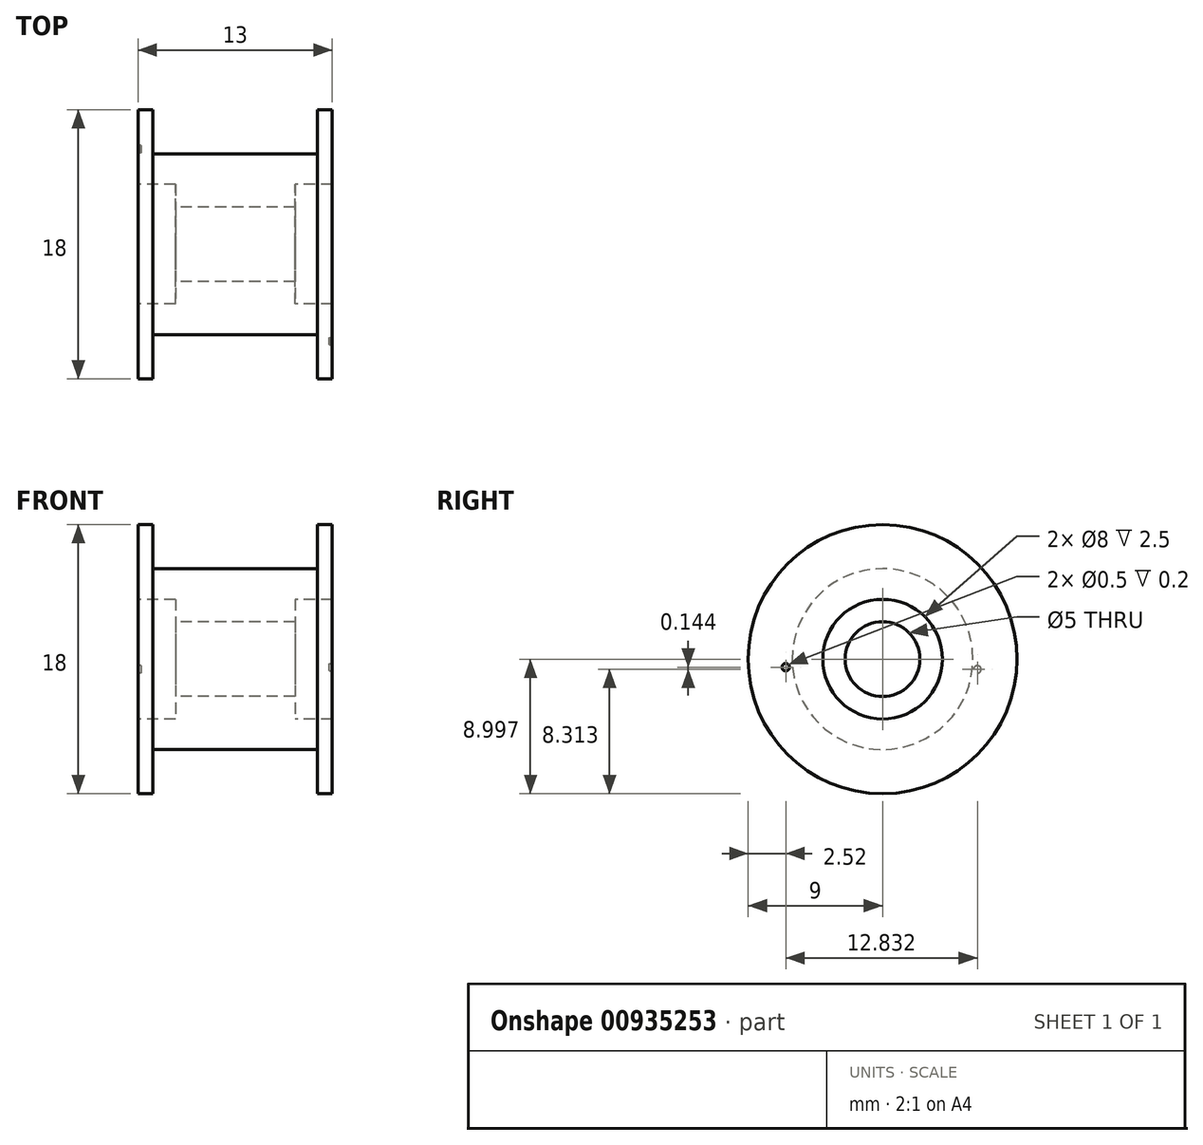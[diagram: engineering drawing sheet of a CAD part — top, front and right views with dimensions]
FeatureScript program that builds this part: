
annotation { "Feature Type Name" : "Feature", "Feature Type Description" : "" }
export const myFeature = defineFeature(function(context is Context, id is Id, definition is map)
    precondition{}
    {
        {
            var Q0;
            Q0=qCreatedBy(makeId("Front.planeOp"),FACE);
            var sketch = newSketch(context, id + "F0", { "sketchPlane" : qUnion([Q0])});
            skLineSegment(sketch, "E0.bottom", {"start": v(-4.63, 6.34) * mm, "end": v(-3.63, 6.34) * mm});
            skLineSegment(sketch, "E0.left", {"start": v(-4.63, 6.34) * mm, "end": v(-4.63, 1.34) * mm});
            skLineSegment(sketch, "E0.right", {"start": v(8.37, 6.34) * mm, "end": v(8.37, 1.34) * mm});
            skLineSegment(sketch, "E1", {"start": v(-3.63, 6.34) * mm, "end": v(-3.63, 1.34) * mm, "construction": true});
            skLineSegment(sketch, "E2", {"start": v(7.37, 6.34) * mm, "end": v(7.37, 1.34) * mm, "construction": true});
            skLineSegment(sketch, "E3", {"start": v(1.87, 3.39) * mm, "end": v(1.87, -2.66) * mm, "construction": true});
            skLineSegment(sketch, "E4", {"start": v(-4.63, 3.39) * mm, "end": v(8.37, 3.39) * mm, "construction": true});
            skLineSegment(sketch, "E5", {"start": v(-3.63, 6.34) * mm, "end": v(-3.63, 3.39) * mm});
            skLineSegment(sketch, "E6", {"start": v(-3.63, 3.39) * mm, "end": v(7.37, 3.39) * mm});
            skLineSegment(sketch, "E7", {"start": v(7.37, 3.39) * mm, "end": v(7.37, 6.34) * mm});
            skLineSegment(sketch, "E8.trimOffspring", {"start": v(7.37, 6.34) * mm, "end": v(8.37, 6.34) * mm});
            skLineSegment(sketch, "E9", {"start": v(-4.63, 1.34) * mm, "end": v(-2.13, 1.34) * mm});
            skLineSegment(sketch, "E10", {"start": v(-2.13, 3.39) * mm, "end": v(-2.13, -2.66) * mm, "construction": true});
            skLineSegment(sketch, "E11", {"start": v(5.87, 3.39) * mm, "end": v(5.87, -2.66) * mm, "construction": true});
            skLineSegment(sketch, "E12", {"start": v(-2.13, 1.34) * mm, "end": v(-2.13, -2.66) * mm});
            skLineSegment(sketch, "E13", {"start": v(-2.13, -2.66) * mm, "end": v(5.87, -2.66) * mm});
            skLineSegment(sketch, "E14", {"start": v(5.87, -2.66) * mm, "end": v(5.87, 1.34) * mm});
            skLineSegment(sketch, "E15", {"start": v(5.87, 1.34) * mm, "end": v(8.37, 1.34) * mm});
            skLineSegment(sketch, "E16.trimOffspring", {"start": v(-2.13, -2.66) * mm, "end": v(5.87, -2.66) * mm, "construction": true});
            skLineSegment(sketch, "E17.trimOffspring", {"start": v(-2.13, -0.16) * mm, "end": v(5.87, -0.16) * mm, "construction": true});
            skSolve(sketch);
        }
        {
            var Q0;
            Q0=makeQuery(id+"F0.imprint","IMPRINT",FACE,{"disambiguationData":[TD([[makeQuery(id+"F0.imprint","IMPRINT",EDGE,{"derivedFrom":sQuery(id+"F0.wireOp",EDGE,"E0.bottom")}),-1.0]])]});
            var Q1;
            Q1=sQuery(id+"F0.wireOp",EDGE,"E13");
            revolve(context, id + "F1", {"surfaceOperationType" : NewSurfaceOperationType.NEW, "entities" : qUnion([Q0]), "axis" : qUnion([Q1]), "revolveType" : RevolveType.FULL});
        }
        {
            var Q0;
            Q0=makeQuery(id+"F1.opRevolve","SWEPT_FACE",FACE,{"disambiguationData":[OSD([sQuery(id+"F0.wireOp",EDGE,"E12")])]});
            var sketch = newSketch(context, id + "F2", { "sketchPlane" : qUnion([Q0])});
            skPoint(sketch, "E18", {"position": v(0, -2.66) * mm});
            skSolve(sketch);
        }
        {
            var Q0;
            Q0=sQuery(id+"F2.wireOp",VERTEX,"E18");
            var Q1;
            Q1=makeQuery(id+"F1.opRevolve","SWEPT_BODY",BODY,{"disambiguationData":[OSD([sQuery(id+"F0.wireOp",EDGE,"E0.bottom"),sQuery(id+"F0.wireOp",EDGE,"E0.left"),sQuery(id+"F0.wireOp",EDGE,"E0.right"),sQuery(id+"F0.wireOp",EDGE,"E5"),sQuery(id+"F0.wireOp",EDGE,"E6"),sQuery(id+"F0.wireOp",EDGE,"E7"),sQuery(id+"F0.wireOp",EDGE,"E8.trimOffspring"),sQuery(id+"F0.wireOp",EDGE,"E9"),sQuery(id+"F0.wireOp",EDGE,"E12"),sQuery(id+"F0.wireOp",EDGE,"E13"),sQuery(id+"F0.wireOp",EDGE,"E14"),sQuery(id+"F0.wireOp",EDGE,"E15")])]});
            hole(context, id + "F3", {"style" : HoleStyle.SIMPLE, "endStyle" : HoleEndStyle.THROUGH, "holeDiameter" : 5 * mm, "majorDiameter" : 4 * mm, "tappedDepth" : 12 * mm, "tapClearance" : 3, "locations" : qUnion([Q0]), "scope" : qUnion([Q1])});
        }
        {
            var Q0;
            Q0=makeQuery(id+"F1.opRevolve","SWEPT_FACE",FACE,{"disambiguationData":[OSD([sQuery(id+"F0.wireOp",EDGE,"E0.right")])]});
            var sketch = newSketch(context, id + "F4", { "sketchPlane" : qUnion([Q0])});
            skPoint(sketch, "E19", {"position": v(-6.48, -3.2) * mm});
            skCircle(sketch, "E20", {"center": v(-6.48, -3.2) * mm, "radius": 0.25 * mm});
            skSolve(sketch);
        }
        {
            var Q0;
            Q0 = qSketchRegion(id + "F4", true);
            extrude(context, id + "F5", {"entities" : qUnion([Q0]), "operationType" : NewBodyOperationType.REMOVE, "oppositeDirection" : true, "depth" : 0.2 * mm, "offsetDistance" : 25 * mm});
        }
        {
            var Q0;
            Q0=makeQuery(id+"F1.opRevolve","SWEPT_FACE",FACE,{"disambiguationData":[OSD([sQuery(id+"F0.wireOp",EDGE,"E0.left")])]});
            var sketch = newSketch(context, id + "F6", { "sketchPlane" : qUnion([Q0])});
            skPoint(sketch, "E21", {"position": v(-6.35, -3.35) * mm});
            skCircle(sketch, "E22", {"center": v(-6.35, -3.35) * mm, "radius": 0.25 * mm});
            skSolve(sketch);
        }
        {
            var Q0;
            Q0=makeQuery(id+"F6.imprint","IMPRINT",FACE,{"disambiguationData":[TD([[makeQuery(id+"F6.imprint","IMPRINT",EDGE,{"derivedFrom":sQuery(id+"F6.wireOp",EDGE,"E22")}),1.0]])]});
            extrude(context, id + "F7", {"entities" : qUnion([Q0]), "operationType" : NewBodyOperationType.REMOVE, "oppositeDirection" : true, "depth" : 0.2 * mm, "offsetDistance" : 25 * mm});
        }
    });
